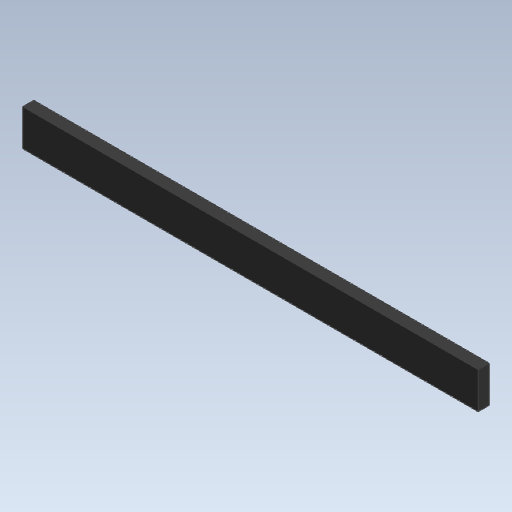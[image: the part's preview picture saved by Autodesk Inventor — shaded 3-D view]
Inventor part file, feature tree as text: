
AUTODESK INVENTOR PART (.ipt)
format: ipt  version: 2020 (Build 240168000, 168)  size: 82,944 bytes
history: native  units: mm
features: other x1, extrude x1
ambient origin geometry x8: Origin, YZ Plane, XZ Plane, XY Plane, X Axis, Y Axis, Z Axis, Center Point
bodies: Body1 (feature_tree)
feature tree (2):
  other  "實體1"
  extrude  "擠出1"  Depth=10.0mm
